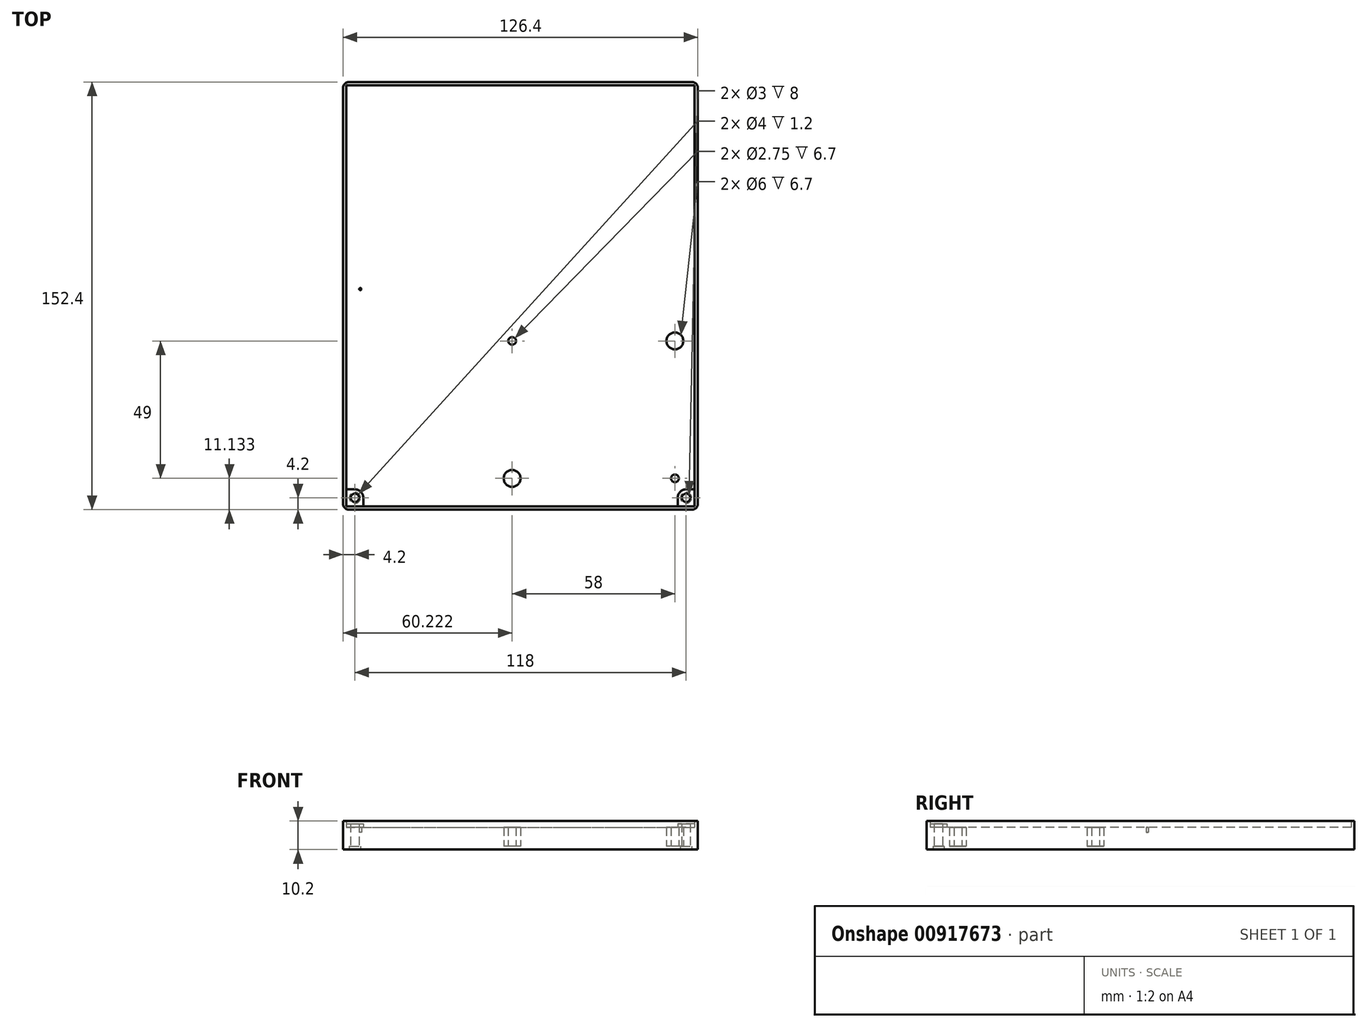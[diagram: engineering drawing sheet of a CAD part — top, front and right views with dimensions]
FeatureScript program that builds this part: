
annotation { "Feature Type Name" : "Feature", "Feature Type Description" : "" }
export const myFeature = defineFeature(function(context is Context, id is Id, definition is map)
    precondition{}
    {
        {
            var Q0;
            Q0=qCreatedBy(makeId("Top.planeOp"),FACE);
            var sketch = newSketch(context, id + "F0", { "sketchPlane" : qUnion([Q0])});
            skLineSegment(sketch, "E0.bottom", {"start": v(-62, 75) * mm, "end": v(62, 75) * mm});
            skLineSegment(sketch, "E0.top", {"start": v(-62, -75) * mm, "end": v(62, -75) * mm});
            skLineSegment(sketch, "E0.left", {"start": v(-62, 75) * mm, "end": v(-62, -75) * mm});
            skLineSegment(sketch, "E0.right", {"start": v(62, 75) * mm, "end": v(62, -75) * mm});
            skLineSegment(sketch, "E1.0", {"start": v(-63.2, -76.2) * mm, "end": v(63.2, -76.2) * mm});
            skLineSegment(sketch, "E1.1", {"start": v(-63.2, 76.2) * mm, "end": v(-63.2, -76.2) * mm});
            skLineSegment(sketch, "E1.2", {"start": v(-63.2, 76.2) * mm, "end": v(63.2, 76.2) * mm});
            skLineSegment(sketch, "E1.3", {"start": v(63.2, 76.2) * mm, "end": v(63.2, -76.2) * mm});
            skPoint(sketch, "E2.visualSharp", {"position": v(-63.2, 76.2) * mm});
            skPoint(sketch, "E3.visualSharp", {"position": v(-62, 75) * mm});
            skPoint(sketch, "E4", {"position": v(62, 0) * mm});
            skPoint(sketch, "E5", {"position": v(0, 75) * mm});
            skLineSegment(sketch, "E6", {"start": v(0, 75) * mm, "end": v(0, -75.03) * mm, "construction": true});
            skLineSegment(sketch, "E7", {"start": v(62, 0) * mm, "end": v(-62, 0) * mm, "construction": true});
            skSolve(sketch);
        }
        {
            var Q0;
            Q0=makeQuery(id+"F0.imprint","IMPRINT",FACE,{"disambiguationData":[TD([[makeQuery(id+"F0.imprint","IMPRINT",EDGE,{"derivedFrom":sQuery(id+"F0.wireOp",EDGE,"E0.bottom")}),1.0]])]});
            extrude(context, id + "F1", {"entities" : qUnion([Q0]), "depth" : 10.2 * mm, "offsetDistance" : 25.4 * mm});
        }
        {
            var Q0;
            Q0=makeQuery(id+"F0.imprint","IMPRINT",FACE,{"disambiguationData":[TD([[makeQuery(id+"F0.imprint","IMPRINT",EDGE,{"derivedFrom":sQuery(id+"F0.wireOp",EDGE,"E0.bottom")}),-1.0]])]});
            var Q1;
            Q1=makeQuery(id+"F0.imprint","IMPRINT",FACE,{"disambiguationData":[TD([[makeQuery(id+"F0.imprint","IMPRINT",EDGE,{"derivedFrom":sQuery(id+"F0.wireOp",EDGE,"11117f73-f199-47b9-847d-04a500e91c59")}),1.0]])]});
            var Q2;
            Q2=makeQuery(id+"F0.imprint","IMPRINT",FACE,{"disambiguationData":[TD([[makeQuery(id+"F0.imprint","IMPRINT",EDGE,{"derivedFrom":sQuery(id+"F0.wireOp",EDGE,"11117f73-f199-47b9-847d-04a500e91c59")}),-1.0]])]});
            var Q3;
            Q3=makeQuery(id+"F0.imprint","IMPRINT",FACE,{"disambiguationData":[TD([[makeQuery(id+"F0.imprint","IMPRINT",EDGE,{"derivedFrom":sQuery(id+"F0.wireOp",EDGE,"3PQHME3d-FfnH-2Ykc-PiKR-dZN34DyuNOqD")}),-1.0]])]});
            var Q4;
            Q4=makeQuery(id+"F0.imprint","IMPRINT",FACE,{"disambiguationData":[TD([[makeQuery(id+"F0.imprint","IMPRINT",EDGE,{"derivedFrom":sQuery(id+"F0.wireOp",EDGE,"3PQHME3d-FfnH-2Ykc-PiKR-dZN34DyuNOqD")}),1.0]])]});
            var Q5;
            Q5=makeQuery(id+"F0.imprint","IMPRINT",FACE,{"disambiguationData":[TD([[makeQuery(id+"F0.imprint","IMPRINT",EDGE,{"derivedFrom":sQuery(id+"F0.wireOp",EDGE,"2941c58d-53f6-455c-ad84-b15755ab7034.0")}),1.0]])]});
            var Q6;
            Q6=makeQuery(id+"F0.imprint","IMPRINT",FACE,{"disambiguationData":[TD([[makeQuery(id+"F0.imprint","IMPRINT",EDGE,{"derivedFrom":sQuery(id+"F0.wireOp",EDGE,"50ba8ca9-27dd-4aff-b00d-4bc875650b6e0.MirrorC")}),-1.0]])]});
            var Q7;
            Q7=makeQuery(id+"F0.imprint","IMPRINT",FACE,{"disambiguationData":[TD([[makeQuery(id+"F0.imprint","IMPRINT",EDGE,{"derivedFrom":sQuery(id+"F0.wireOp",EDGE,"5cd76852-fb94-406f-bd0e-9de124dfac3c0.MirrorC")}),-1.0]])]});
            var Q8;
            Q8=makeQuery(id+"F0.imprint","IMPRINT",FACE,{"disambiguationData":[TD([[makeQuery(id+"F0.imprint","IMPRINT",EDGE,{"derivedFrom":sQuery(id+"F0.wireOp",EDGE,"0279cc56-c578-4efb-90db-0dc0a5edd46d0.MirrorC")}),1.0]])]});
            var Q9;
            Q9=makeQuery(id+"F0.imprint","IMPRINT",FACE,{"disambiguationData":[TD([[makeQuery(id+"F0.imprint","IMPRINT",EDGE,{"derivedFrom":sQuery(id+"F0.wireOp",EDGE,"0279cc56-c578-4efb-90db-0dc0a5edd46d0.MirrorC")}),-1.0]])]});
            var Q10;
            Q10=makeQuery(id+"F0.imprint","IMPRINT",FACE,{"disambiguationData":[TD([[makeQuery(id+"F0.imprint","IMPRINT",EDGE,{"derivedFrom":sQuery(id+"F0.wireOp",EDGE,"68778e04-4f42-4938-ac99-ffc00e64d5e10.MirrorC")}),-1.0]])]});
            var Q11;
            Q11=makeQuery(id+"F0.imprint","IMPRINT",FACE,{"disambiguationData":[TD([[makeQuery(id+"F0.imprint","IMPRINT",EDGE,{"derivedFrom":sQuery(id+"F0.wireOp",EDGE,"68778e04-4f42-4938-ac99-ffc00e64d5e10.MirrorC")}),1.0]])]});
            extrude(context, id + "F2", {"entities" : qUnion([Q0, Q1, Q2, Q3, Q4, Q5, Q6, Q7, Q8, Q9, Q10, Q11]), "operationType" : NewBodyOperationType.ADD, "depth" : 1.2 * mm, "offsetDistance" : 25.4 * mm});
        }
        {
            var Q0;
            {var subQ0=sQuery(id+"F0.wireOp",EDGE,"E1.3");var subQ1=sQuery(id+"F0.wireOp",EDGE,"E1.0");Q0=makeQuery(id+"F2.boolean.opBoolean","MERGE",EDGE,{"derivedFrom":[makeQuery(id+"F1.opExtrude","SWEPT_EDGE",EDGE,{"disambiguationData":[OSD([subQ1,subQ0])]}),makeQuery(id+"F2.opExtrude","SWEPT_EDGE",EDGE,{"disambiguationData":[OSD([subQ1,subQ0])]})]});}
            var Q1;
            {var subQ0=sQuery(id+"F0.wireOp",EDGE,"E1.2");var subQ1=sQuery(id+"F0.wireOp",EDGE,"E1.1");Q1=makeQuery(id+"F2.boolean.opBoolean","MERGE",EDGE,{"derivedFrom":[makeQuery(id+"F1.opExtrude","SWEPT_EDGE",EDGE,{"disambiguationData":[OSD([subQ1,subQ0])]}),makeQuery(id+"F2.opExtrude","SWEPT_EDGE",EDGE,{"disambiguationData":[OSD([subQ1,subQ0])]})]});}
            var Q2;
            {var subQ0=sQuery(id+"F0.wireOp",EDGE,"E1.3");var subQ1=sQuery(id+"F0.wireOp",EDGE,"E1.2");Q2=makeQuery(id+"F2.boolean.opBoolean","MERGE",EDGE,{"derivedFrom":[makeQuery(id+"F1.opExtrude","SWEPT_EDGE",EDGE,{"disambiguationData":[OSD([subQ1,subQ0])]}),makeQuery(id+"F2.opExtrude","SWEPT_EDGE",EDGE,{"disambiguationData":[OSD([subQ1,subQ0])]})]});}
            var Q3;
            {var subQ0=sQuery(id+"F0.wireOp",EDGE,"E1.1");var subQ1=sQuery(id+"F0.wireOp",EDGE,"E1.0");Q3=makeQuery(id+"F2.boolean.opBoolean","MERGE",EDGE,{"derivedFrom":[makeQuery(id+"F1.opExtrude","SWEPT_EDGE",EDGE,{"disambiguationData":[OSD([subQ1,subQ0])]}),makeQuery(id+"F2.opExtrude","SWEPT_EDGE",EDGE,{"disambiguationData":[OSD([subQ1,subQ0])]})]});}
            fillet(context, id + "F3", {"entities" : qUnion([Q0, Q1, Q2, Q3]), "radius" : 2 * mm, "tangentPropagation" : true, "allowEdgeOverflow" : false});
        }
        {
            var Q0;
            {var subQ0=sQuery(id+"F0.wireOp",EDGE,"E0.right");var subQ1=sQuery(id+"F0.wireOp",EDGE,"E0.left");var subQ2=sQuery(id+"F0.wireOp",EDGE,"E0.top");var subQ3=sQuery(id+"F0.wireOp",EDGE,"E0.bottom");Q0=makeQuery(id+"F2.boolean.opBoolean","MERGE",FACE,{"derivedFrom":[makeQuery(id+"F1.opExtrude","CAP_FACE",FACE,{"disambiguationData":[OSD([subQ3,subQ2,subQ1,subQ0,sQuery(id+"F0.wireOp",EDGE,"E1.0"),sQuery(id+"F0.wireOp",EDGE,"E1.1"),sQuery(id+"F0.wireOp",EDGE,"E1.2"),sQuery(id+"F0.wireOp",EDGE,"E1.3")])],"isStart":true}),makeQuery(id+"F2.opExtrude","CAP_FACE",FACE,{"disambiguationData":[OSD([subQ3,subQ2,subQ1,subQ0])],"isStart":true})]});}
            var sketch = newSketch(context, id + "F4", { "sketchPlane" : qUnion([Q0])});
            skLineSegment(sketch, "E8.bottom", {"start": v(62, 75) * mm, "end": v(56, 75) * mm});
            skLineSegment(sketch, "E8.top", {"start": v(62, 69) * mm, "end": v(59, 69) * mm});
            skLineSegment(sketch, "E8.left", {"start": v(62, 75) * mm, "end": v(62, 69) * mm});
            skLineSegment(sketch, "E8.right", {"start": v(56, 75) * mm, "end": v(56, 72) * mm});
            skLineSegment(sketch, "E9", {"start": v(59, 69) * mm, "end": v(59, 75) * mm, "construction": true});
            skCircle(sketch, "E10", {"center": v(59, 72) * mm, "radius": 1.5 * mm});
            skLineSegment(sketch, "E11", {"start": v(0, -76.2) * mm, "end": v(0, 76.2) * mm, "construction": true});
            skPoint(sketch, "E12.visualSharp", {"position": v(56, 69) * mm});
            skArc(sketch, "E12.filletArc", {"start": v(56, 72) * mm, "mid": v(56.88, 69.88) * mm, "end": v(59, 69) * mm});
            skLineSegment(sketch, "E13.MirrorCS", {"start": v(-62, 75) * mm, "end": v(-62, 69) * mm});
            skLineSegment(sketch, "E14.MirrorCS", {"start": v(-62, 69) * mm, "end": v(-59, 69) * mm});
            skArc(sketch, "E15.MirrorCS", {"start": v(-56, 72) * mm, "mid": v(-56.88, 69.88) * mm, "end": v(-59, 69) * mm});
            skLineSegment(sketch, "E16.MirrorCS", {"start": v(-56, 75) * mm, "end": v(-56, 72) * mm});
            skLineSegment(sketch, "E17.MirrorCS", {"start": v(-62, 75) * mm, "end": v(-56, 75) * mm});
            skCircle(sketch, "E18.MirrorC", {"center": v(-59, 72) * mm, "radius": 1.5 * mm});
            skLineSegment(sketch, "E19.MirrorCS", {"start": v(-59, 69) * mm, "end": v(-59, 75) * mm, "construction": true});
            skSolve(sketch);
        }
        {
            var Q0;
            Q0=makeQuery(id+"F4.imprint","IMPRINT",FACE,{"disambiguationData":[TD([[makeQuery(id+"F4.imprint","IMPRINT",EDGE,{"derivedFrom":sQuery(id+"F4.wireOp",EDGE,"E8.bottom")}),1.0]])]});
            var Q1;
            Q1=makeQuery(id+"F4.imprint","IMPRINT",FACE,{"disambiguationData":[TD([[makeQuery(id+"F4.imprint","IMPRINT",EDGE,{"derivedFrom":sQuery(id+"F4.wireOp",EDGE,"E10")}),1.0]])]});
            var Q2;
            Q2=makeQuery(id+"F4.imprint","IMPRINT",FACE,{"disambiguationData":[TD([[makeQuery(id+"F4.imprint","IMPRINT",EDGE,{"derivedFrom":sQuery(id+"F4.wireOp",EDGE,"E13.MirrorCS")}),1.0]])]});
            var Q3;
            Q3=makeQuery(id+"F4.imprint","IMPRINT",FACE,{"disambiguationData":[TD([[makeQuery(id+"F4.imprint","IMPRINT",EDGE,{"derivedFrom":sQuery(id+"F4.wireOp",EDGE,"E18.MirrorC")}),-1.0]])]});
            extrude(context, id + "F5", {"entities" : qUnion([Q0, Q1, Q2, Q3]), "operationType" : NewBodyOperationType.ADD, "oppositeDirection" : true, "depth" : 9.2 * mm, "offsetDistance" : 25 * mm});
        }
        {
            var Q0;
            Q0=sQuery(id+"F4.wireOp",VERTEX,"E10.center");
            var Q1;
            Q1=sQuery(id+"F4.wireOp",VERTEX,"E15.MirrorCS.center");
            var Q2;
            Q2=makeQuery(id+"F1.opExtrude","SWEPT_BODY",BODY,{"disambiguationData":[OSD([sQuery(id+"F0.wireOp",EDGE,"E0.bottom"),sQuery(id+"F0.wireOp",EDGE,"E0.top"),sQuery(id+"F0.wireOp",EDGE,"E0.left"),sQuery(id+"F0.wireOp",EDGE,"E0.right"),sQuery(id+"F0.wireOp",EDGE,"E1.0"),sQuery(id+"F0.wireOp",EDGE,"E1.1"),sQuery(id+"F0.wireOp",EDGE,"E1.2"),sQuery(id+"F0.wireOp",EDGE,"E1.3")])]});
            hole(context, id + "F6", {"style" : HoleStyle.C_BORE, "endStyle" : HoleEndStyle.THROUGH, "holeDiameter" : 3 * mm, "cBoreDiameter" : 4 * mm, "cBoreDepth" : 1.2 * mm, "majorDiameter" : 5 * mm, "isTappedThrough" : true, "tappedDepth" : 12 * mm, "tapClearance" : 3, "locations" : qUnion([Q0, Q1]), "scope" : qUnion([Q2])});
        }
        {
            var Q0;
            Q0=makeQuery(id+"F2.opExtrude","CAP_FACE",FACE,{"disambiguationData":[OSD([sQuery(id+"F0.wireOp",EDGE,"E0.bottom"),sQuery(id+"F0.wireOp",EDGE,"E0.top"),sQuery(id+"F0.wireOp",EDGE,"E0.left"),sQuery(id+"F0.wireOp",EDGE,"E0.right")])],"isStart":false});
            var sketch = newSketch(context, id + "F7", { "sketchPlane" : qUnion([Q0])});
            skCircle(sketch, "E20", {"center": v(-2.98, -16.07) * mm, "radius": 1.38 * mm});
            skCircle(sketch, "E21.0", {"center": v(-2.98, -16.07) * mm, "radius": 3 * mm});
            skLineSegment(sketch, "E22", {"start": v(-2.98, -16.07) * mm, "end": v(55.02, -16.07) * mm, "construction": true});
            skLineSegment(sketch, "E23", {"start": v(55.02, -16.07) * mm, "end": v(55.02, -65.07) * mm, "construction": true});
            skLineSegment(sketch, "E24", {"start": v(55.02, -65.07) * mm, "end": v(-2.98, -65.07) * mm, "construction": true});
            skLineSegment(sketch, "E25", {"start": v(-2.98, -65.07) * mm, "end": v(-2.98, -16.07) * mm, "construction": true});
            skLineSegment(sketch, "E26", {"start": v(26.02, -16.07) * mm, "end": v(26.02, -65.07) * mm, "construction": true});
            skLineSegment(sketch, "E27", {"start": v(-2.98, -40.57) * mm, "end": v(55.02, -40.57) * mm, "construction": true});
            skCircle(sketch, "E28.MirrorC", {"center": v(55.02, -16.07) * mm, "radius": 3 * mm});
            skCircle(sketch, "E29.MirrorC", {"center": v(55.02, -16.07) * mm, "radius": 1.38 * mm});
            skCircle(sketch, "E30.MirrorC", {"center": v(55.02, -65.07) * mm, "radius": 3 * mm});
            skCircle(sketch, "E31.MirrorC", {"center": v(55.02, -65.07) * mm, "radius": 1.38 * mm});
            skCircle(sketch, "E32.MirrorC", {"center": v(-2.98, -65.07) * mm, "radius": 3 * mm});
            skCircle(sketch, "E33.MirrorC", {"center": v(-2.98, -65.07) * mm, "radius": 1.38 * mm});
            skLineSegment(sketch, "E34.bottom", {"start": v(-57.05, 2.41) * mm, "end": v(-14.05, 2.41) * mm, "construction": true});
            skLineSegment(sketch, "E34.top", {"start": v(-57.05, -64.59) * mm, "end": v(-14.05, -64.59) * mm, "construction": true});
            skLineSegment(sketch, "E34.left", {"start": v(-57.05, 2.41) * mm, "end": v(-57.05, -64.59) * mm, "construction": true});
            skLineSegment(sketch, "E34.right", {"start": v(-14.05, 2.41) * mm, "end": v(-14.05, -64.59) * mm, "construction": true});
            skCircle(sketch, "E35", {"center": v(-57.05, 2.41) * mm, "radius": 0.4 * mm});
            skSolve(sketch);
        }
        {
            var Q0;
            Q0=makeQuery(id+"F7.imprint","IMPRINT",FACE,{"disambiguationData":[TD([[makeQuery(id+"F7.imprint","IMPRINT",EDGE,{"derivedFrom":sQuery(id+"F7.wireOp",EDGE,"E28.MirrorC")}),-1.0]])]});
            var Q1;
            Q1=makeQuery(id+"F7.imprint","IMPRINT",FACE,{"disambiguationData":[TD([[makeQuery(id+"F7.imprint","IMPRINT",EDGE,{"derivedFrom":sQuery(id+"F7.wireOp",EDGE,"E20")}),-1.0]])]});
            var Q2;
            Q2=makeQuery(id+"F7.imprint","IMPRINT",FACE,{"disambiguationData":[TD([[makeQuery(id+"F7.imprint","IMPRINT",EDGE,{"derivedFrom":sQuery(id+"F7.wireOp",EDGE,"E32.MirrorC")}),-1.0]])]});
            var Q3;
            Q3=makeQuery(id+"F7.imprint","IMPRINT",FACE,{"disambiguationData":[TD([[makeQuery(id+"F7.imprint","IMPRINT",EDGE,{"derivedFrom":sQuery(id+"F7.wireOp",EDGE,"E30.MirrorC")}),1.0]])]});
            extrude(context, id + "F8", {"entities" : qUnion([Q0, Q1, Q2, Q3]), "operationType" : NewBodyOperationType.ADD, "depth" : 6.7 * mm, "offsetDistance" : 25 * mm});
        }
        {
            var Q0;
            Q0=makeQuery(id+"F7.imprint","IMPRINT",FACE,{"disambiguationData":[TD([[makeQuery(id+"F7.imprint","IMPRINT",EDGE,{"derivedFrom":sQuery(id+"F7.wireOp",EDGE,"E35")}),1.0]])]});
            extrude(context, id + "F9", {"entities" : qUnion([Q0]), "operationType" : NewBodyOperationType.ADD, "depth" : 5 * mm, "offsetDistance" : 25 * mm});
        }
    });
